# Revit family: LD4FD
name_source: partatom
category: Lighting Fixtures
revit_build: Autodesk Revit Architecture 2012 (Build: 20110309_2315(x64)
units: mm (PartAtom-declared; Revit-internal decimal feet)

## types (3) — shared parameters
Backbox = Steel
Color Filter = 16777215
Default Elevation = 48.000"
Description = 4' Direct/Indirect LED Wall Mount Cylinder
Dimming Lamp Color Temperature Shift = <None>
Emit from Line Length = 24.000"
Glass = Glass
Lamp = 1
Manufacturer = prescolite
Manufacturer Fax = 864-678-1415
Model = LD4FD
Product Documentation Link = http://www.prescolite.com
Product Page URL = http://www.prescolite.com
Tilt Angle = 180.00°
URL = http://www.prescolite.com
Wattage Comments = 8-15W

## per-type parameters (varying)
| type | Photometric Web File |
| LD4 Wall Mount Cylinder, Spot Up / Flood Down, 600 Lumens, 50K | 8902.IES |
| LD4 Wall Mount Cylinder, Flood Down, 600 Lumens, 50K | 8898.IES |
| LD4 Wall Mount Cylinder, Spot Down, 600 Lumens, 50K | 8899.IES |

## geometry (parser evidence)
native form markers: Sweep x2
no freeform markers — native parametric forms only
